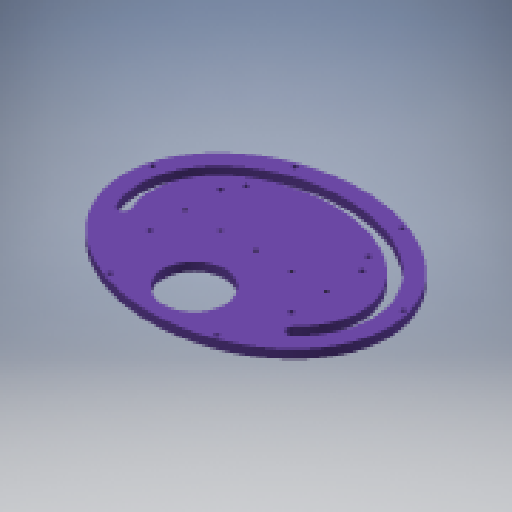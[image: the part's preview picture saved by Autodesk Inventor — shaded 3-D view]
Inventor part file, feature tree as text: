
AUTODESK INVENTOR PART (.ipt)
format: ipt  version: 2024.3 (Build 283343000, 343)  size: 407,552 bytes
history: native  units: mm
features: sketch x8, projected_geometry x4, extrude x3, hole x3, reference x3, other x2, plane x1, sweep x1
ambient origin geometry x8: Origin, YZ Plane, XZ Plane, XY Plane, X Axis, Y Axis, Z Axis, Center Point
bodies: Volumenkörper1 (feature_tree)
feature tree (25):
  extrude  "Extrusion1"  Depth=240.0mm
  extrude  "Extrusion2"  Depth=10.0mm
  hole  "Bohrung1"  [1 undecoded]
  hole  "Bohrung2"  [1 undecoded]
  extrude  "Extrusion3"  Depth=12.894099mm
  sketch  "Skizze6"  dims[d12=90.0deg d13=12.894099mm]
  plane  "Arbeitsebene2"
  sweep  "Sweeping1"
  sketch  "Skizze8"  dims[d16=0.0mm d17=0.0mm]
  hole  "Bohrung3"  [1 undecoded]
  sketch  "Skizze2"  dims[d0=300.0mm d1=240.0mm]
  projected_geometry  "Projizierte Kontur1"
  sketch  "Skizze3"  dims[d2=10.0mm d3=0.0mm d7=18.5mm]
  reference  "Referenz1"
  sketch  "Skizze4"  dims[d8=18.5mm d9=31.5mm]
  sketch  "Skizze5"  dims[d10=31.5mm d11=45.0deg]
  reference  "Referenz2"
  reference  "Referenz3"
  projected_geometry  "Projizierte Kontur2"
  sketch  "Skizze7"  dims[d14=30.0deg d15=15.0deg]
  projected_geometry  "Projizierte Kontur3"
  projected_geometry  "Projizierte Kontur4"
  sketch  "Skizze9"  dims[d18=5.2mm d19=6.0mm d20=4.0mm d21=2.0mm d22=90.0deg d23=8.0mm d24=20.594885mm d25=80.0mm d26=160.0mm d27=5.2mm d28=10.0mm d29=4.0mm d30=2.0mm d31=90.0deg d32=14.2mm d33=20.594885mm d34=70.0mm d35=70.0mm d36=10.0mm d37=0.0mm d38=95.0mm d39=125.0mm d40=90.0deg d41=13.0mm d42=0.0mm d43=0.0mm d44=90.0deg d47=80.0mm d48=160.0mm d49=4.134mm d50=10.0mm d51=4.0mm d52=2.0mm d53=90.0deg d54=8.0mm d55=20.594885mm]
  other  "<path> - Kompass, Gehäuse\24_0497_0001.iam"
  other  "24_0497_0001.iam"
note: 3 required parameter values undecoded (feature->parameter linkage not recoverable at this tier; creation-order binding heuristic only, values carry confidence <= 0.55)
note: 1 file-system path scrubbed to <path> (originals preserved in map.json)
